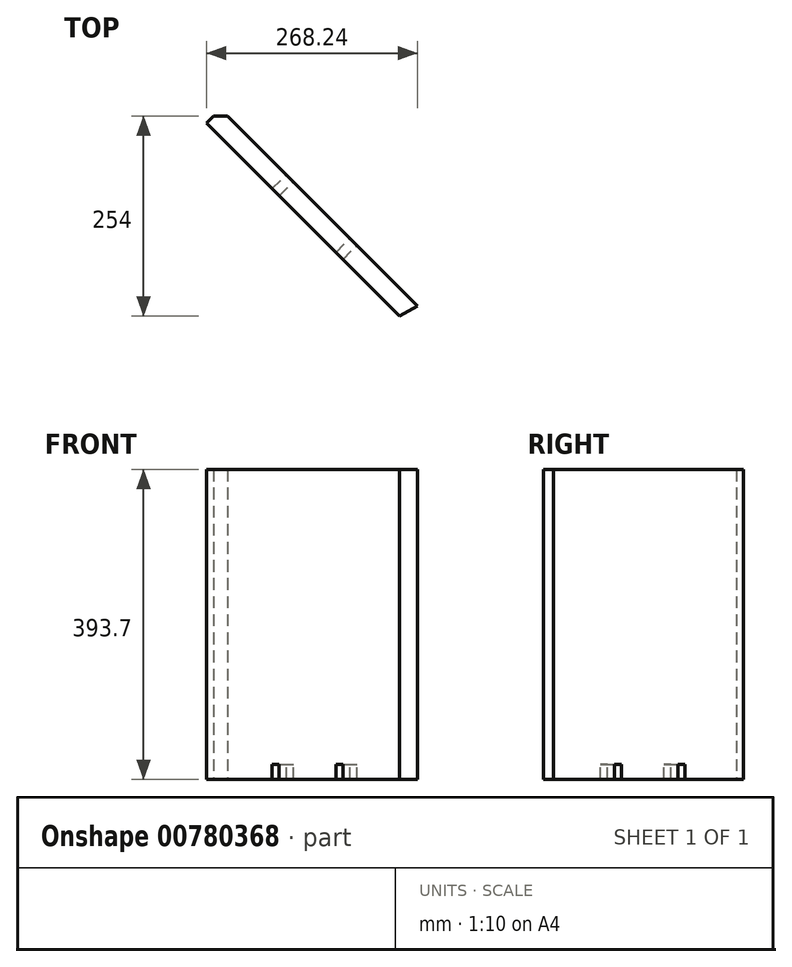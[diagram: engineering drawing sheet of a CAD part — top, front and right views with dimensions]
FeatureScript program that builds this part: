
annotation { "Feature Type Name" : "Feature", "Feature Type Description" : "" }
export const myFeature = defineFeature(function(context is Context, id is Id, definition is map)
    precondition{}
    {
        {
            var Q0;
            Q0=qCreatedBy(makeId("Top.planeOp"),FACE);
            var sketch = newSketch(context, id + "F0", { "sketchPlane" : qUnion([Q0])});
            skLineSegment(sketch, "E0", {"start": v(-279.89, 254) * mm, "end": v(278.91, 254) * mm});
            skLineSegment(sketch, "E1", {"start": v(278.91, 254) * mm, "end": v(532.91, 0) * mm});
            skLineSegment(sketch, "E2.MirrorCS", {"start": v(-279.89, -254) * mm, "end": v(278.91, -254) * mm});
            skLineSegment(sketch, "E3.MirrorCS", {"start": v(278.91, -254) * mm, "end": v(532.91, 0) * mm});
            skLineSegment(sketch, "E4.0", {"start": v(-288.87, 245.02) * mm, "end": v(-43.85, 0) * mm});
            skLineSegment(sketch, "E5.0", {"start": v(-261.93, 254) * mm, "end": v(-20.63, 12.7) * mm});
            skLineSegment(sketch, "E6.MirrorCS", {"start": v(-261.93, -254) * mm, "end": v(-20.63, -12.7) * mm});
            skLineSegment(sketch, "E7.MirrorCS", {"start": v(-288.87, -245.02) * mm, "end": v(-43.85, 0) * mm});
            skLineSegment(sketch, "E8.0", {"start": v(-20.63, -12.7) * mm, "end": v(520.21, -12.7) * mm});
            skLineSegment(sketch, "E9.0", {"start": v(-20.63, 12.7) * mm, "end": v(520.21, 12.7) * mm});
            skLineSegment(sketch, "E10", {"start": v(-43.85, 0) * mm, "end": v(-20.63, 12.7) * mm});
            skLineSegment(sketch, "E11", {"start": v(-43.85, 0) * mm, "end": v(-20.63, -12.7) * mm});
            skLineSegment(sketch, "E12", {"start": v(-115.7, -71.84) * mm, "end": v(-97.73, -89.8) * mm});
            skLineSegment(sketch, "E13.0", {"start": v(-124.67, -80.82) * mm, "end": v(-106.71, -98.78) * mm});
            skLineSegment(sketch, "E14", {"start": v(-279.89, 254) * mm, "end": v(-533.89, 0) * mm});
            skLineSegment(sketch, "E15", {"start": v(-533.89, 0) * mm, "end": v(-279.89, -254) * mm});
            skLineSegment(sketch, "E16", {"start": v(-533.89, 0) * mm, "end": v(532.91, 0) * mm, "construction": true});
            skLineSegment(sketch, "E17.MirrorCS", {"start": v(-124.67, 80.82) * mm, "end": v(-106.71, 98.78) * mm});
            skLineSegment(sketch, "E18.MirrorCS", {"start": v(-115.7, 71.84) * mm, "end": v(-97.73, 89.8) * mm});
            skLineSegment(sketch, "E19", {"start": v(80.97, 12.7) * mm, "end": v(80.97, -12.7) * mm});
            skLineSegment(sketch, "E20.0", {"start": v(93.67, 12.7) * mm, "end": v(93.67, -12.7) * mm});
            skLineSegment(sketch, "E21", {"start": v(-196.51, 152.66) * mm, "end": v(-178.55, 170.62) * mm});
            skLineSegment(sketch, "E22.0", {"start": v(-205.5, 161.64) * mm, "end": v(-187.53, 179.6) * mm});
            skLineSegment(sketch, "E23.MirrorCS", {"start": v(-196.51, -152.66) * mm, "end": v(-178.55, -170.62) * mm});
            skLineSegment(sketch, "E24.MirrorCS", {"start": v(-205.5, -161.64) * mm, "end": v(-187.53, -179.6) * mm});
            skSolve(sketch);
        }
        {
            var Q0;
            {var subQ7=sQuery(id+"F0.wireOp",EDGE,"E22.0");Q0=makeQuery(id+"F0.imprint","IMPRINT",FACE,{"disambiguationData":[TD([[makeQuery(id+"F0.imprint","IMPRINT",EDGE,{"derivedFrom":subQ7}),1.0]])]});}
            var Q1;
            {var subQ0=sQuery(id+"F0.wireOp",EDGE,"E21");Q1=makeQuery(id+"F0.imprint","IMPRINT",FACE,{"disambiguationData":[TD([[makeQuery(id+"F0.imprint","IMPRINT",EDGE,{"derivedFrom":subQ0}),1.0]])]});}
            var Q2;
            {var subQ0=sQuery(id+"F0.wireOp",EDGE,"E17.MirrorCS");Q2=makeQuery(id+"F0.imprint","IMPRINT",FACE,{"disambiguationData":[TD([[makeQuery(id+"F0.imprint","IMPRINT",EDGE,{"derivedFrom":subQ0}),1.0]])]});}
            var Q3;
            {var subQ0=sQuery(id+"F0.wireOp",EDGE,"E17.MirrorCS");Q3=makeQuery(id+"F0.imprint","IMPRINT",FACE,{"disambiguationData":[TD([[makeQuery(id+"F0.imprint","IMPRINT",EDGE,{"derivedFrom":subQ0}),-1.0]])]});}
            var Q4;
            {var subQ0=sQuery(id+"F0.wireOp",EDGE,"E10");Q4=makeQuery(id+"F0.imprint","IMPRINT",FACE,{"disambiguationData":[TD([[makeQuery(id+"F0.imprint","IMPRINT",EDGE,{"derivedFrom":subQ0}),1.0]])]});}
            extrude(context, id + "F1", {"entities" : qUnion([Q0, Q1, Q2, Q3, Q4]), "depth" : 374.65 * mm, "offsetDistance" : 25.4 * mm});
        }
        {
            var Q0;
            {var subQ0=sQuery(id+"F0.wireOp",EDGE,"E10");Q0=makeQuery(id+"F0.imprint","IMPRINT",FACE,{"disambiguationData":[TD([[makeQuery(id+"F0.imprint","IMPRINT",EDGE,{"derivedFrom":subQ0}),1.0]])]});}
            var Q1;
            {var subQ0=sQuery(id+"F0.wireOp",EDGE,"E17.MirrorCS");Q1=makeQuery(id+"F0.imprint","IMPRINT",FACE,{"disambiguationData":[TD([[makeQuery(id+"F0.imprint","IMPRINT",EDGE,{"derivedFrom":subQ0}),1.0]])]});}
            var Q2;
            {var subQ7=sQuery(id+"F0.wireOp",EDGE,"E22.0");Q2=makeQuery(id+"F0.imprint","IMPRINT",FACE,{"disambiguationData":[TD([[makeQuery(id+"F0.imprint","IMPRINT",EDGE,{"derivedFrom":subQ7}),1.0]])]});}
            extrude(context, id + "F2", {"entities" : qUnion([Q0, Q1, Q2]), "operationType" : NewBodyOperationType.ADD, "oppositeDirection" : true, "depth" : 19.05 * mm, "offsetDistance" : 25.4 * mm});
        }
    });
